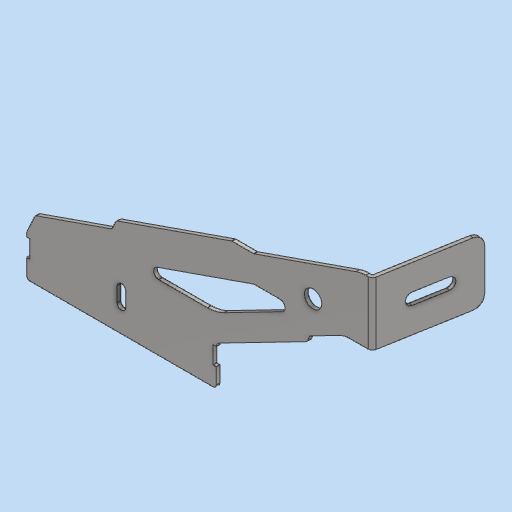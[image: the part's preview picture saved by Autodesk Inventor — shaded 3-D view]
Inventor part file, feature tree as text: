
AUTODESK INVENTOR PART (.ipt)
format: ipt  version: 2023 (Build 270158000, 158)  size: 578,560 bytes
history: native  units: mm
features: other x3, extrude x1, plane x1
ambient origin geometry x8: Origin, YZ Plane, XZ Plane, XY Plane, X Axis, Y Axis, Z Axis, Center Point
bodies: Body1 (feature_tree)
feature tree (5):
  other  "實體1"
  extrude  "擠出1"  Depth=130.0mm
  other  "折彎零件1"
  plane  "工作平面1"
  other  "定義1"
